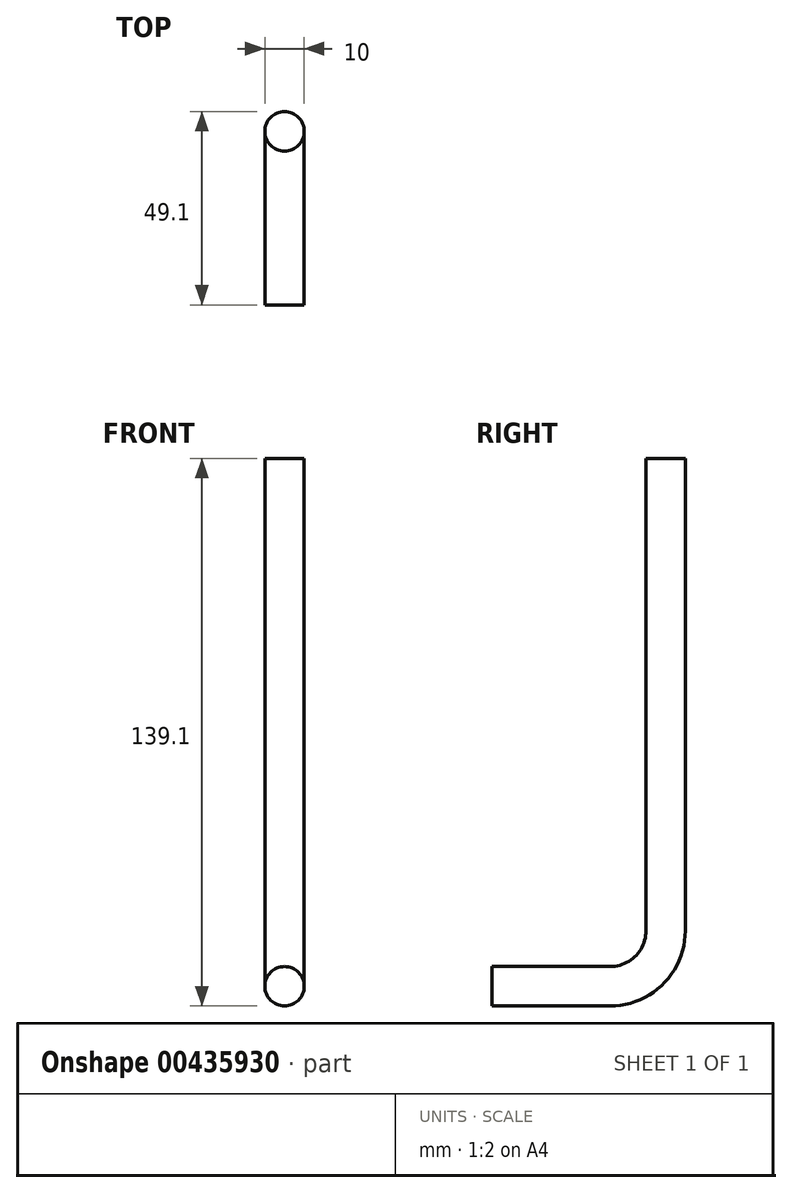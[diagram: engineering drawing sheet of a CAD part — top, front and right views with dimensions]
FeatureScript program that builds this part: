
annotation { "Feature Type Name" : "Feature", "Feature Type Description" : "" }
export const myFeature = defineFeature(function(context is Context, id is Id, definition is map)
    precondition{}
    {
        {
            var Q0;
            Q0=qCreatedBy(makeId("Front.planeOp"),FACE);
            var sketch = newSketch(context, id + "F0", { "sketchPlane" : qUnion([Q0])});
            skCircle(sketch, "E0", {"center": v(0, 0) * mm, "radius": 5 * mm});
            skSolve(sketch);
        }
        {
            var Q0;
            Q0=makeQuery(id+"F0.imprint","IMPRINT",FACE,{"disambiguationData":[TD([[makeQuery(id+"F0.imprint","IMPRINT",EDGE,{"derivedFrom":sQuery(id+"F0.wireOp",EDGE,"E0")}),1.0]])]});
            extrude(context, id + "F1", {"entities" : qUnion([Q0]), "depth" : 30 * mm});
        }
        {
            var Q0;
            Q0=qCreatedBy(makeId("Front.planeOp"),FACE);
            var sketch = newSketch(context, id + "F2", { "sketchPlane" : qUnion([Q0])});
            skLineSegment(sketch, "E1", {"start": v(0, 0) * mm, "end": v(0, 14.1) * mm});
            skLineSegment(sketch, "E2", {"start": v(0, 14.1) * mm, "end": v(-21.3, 14.1) * mm});
            skSolve(sketch);
        }
        {
            var Q0;
            Q0=makeQuery(id+"F1.opExtrude","CAP_FACE",FACE,{"disambiguationData":[OSD([sQuery(id+"F0.wireOp",EDGE,"E0")])],"isStart":true});
            var Q1;
            Q1=sQuery(id+"F2.wireOp",EDGE,"E2");
            revolve(context, id + "F3", {"operationType" : NewBodyOperationType.ADD, "entities" : qUnion([Q0]), "axis" : qUnion([Q1]), "revolveType" : RevolveType.ONE_DIRECTION, "oppositeDirection" : true, "angle" : 90 * degree});
        }
        {
            var Q0;
            Q0=makeQuery(id+"F3.opRevolve","CAP_FACE",FACE,{"disambiguationData":[OSD([sQuery(id+"F0.wireOp",EDGE,"E0")])],"isStart":false});
            extrude(context, id + "F4", {"entities" : qUnion([Q0]), "operationType" : NewBodyOperationType.ADD, "depth" : 120 * mm});
        }
    });
